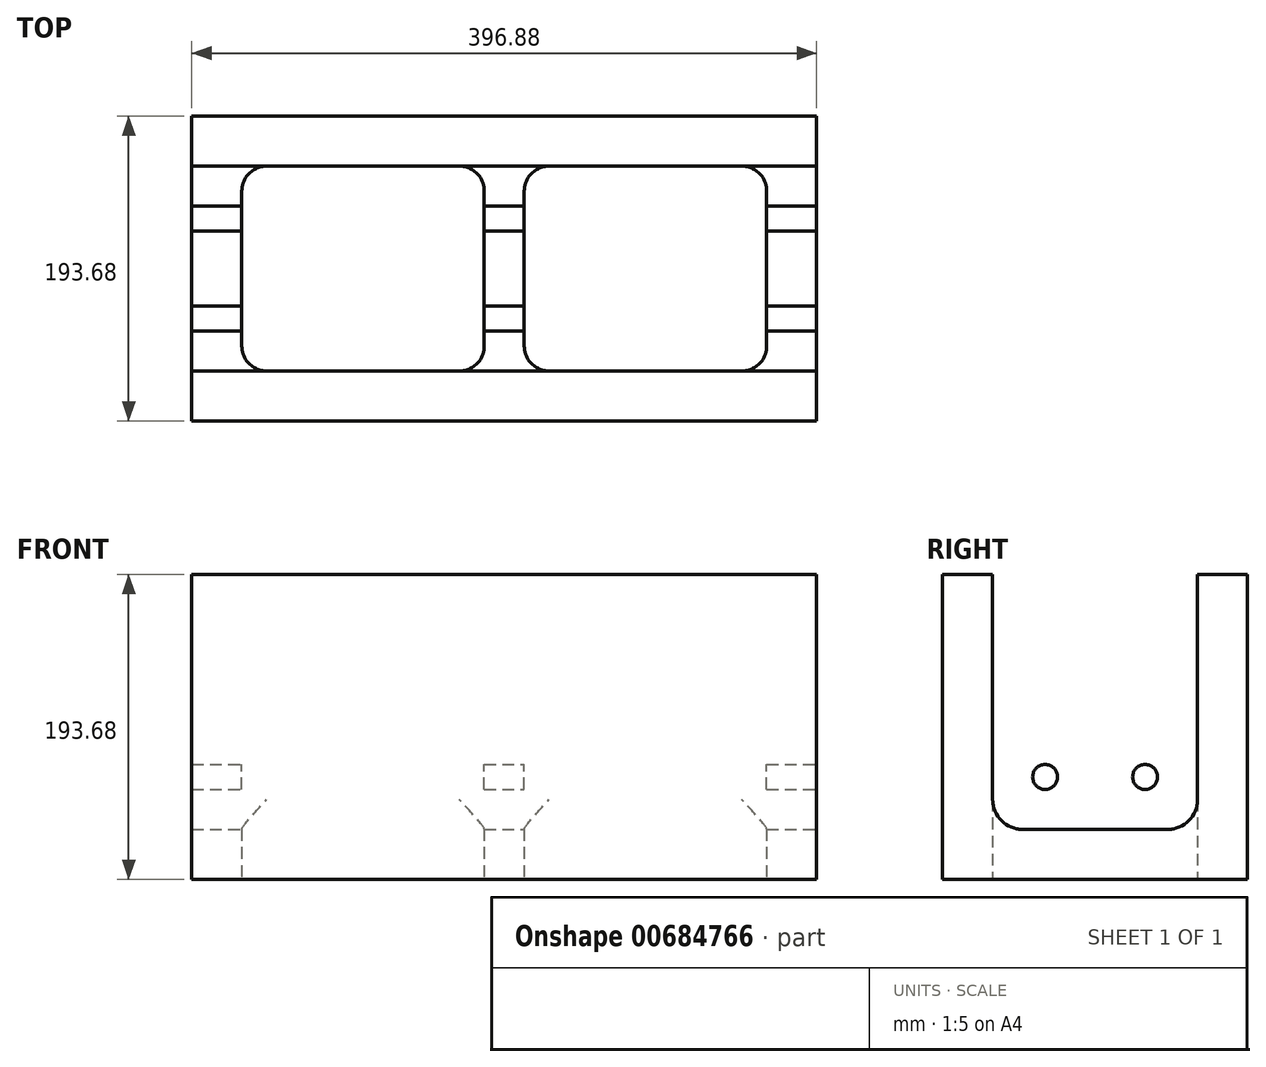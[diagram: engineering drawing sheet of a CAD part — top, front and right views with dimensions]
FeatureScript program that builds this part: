
annotation { "Feature Type Name" : "Feature", "Feature Type Description" : "" }
export const myFeature = defineFeature(function(context is Context, id is Id, definition is map)
    precondition{}
    {
        {
            var Q0;
            Q0=qCreatedBy(makeId("Top.planeOp"),FACE);
            var sketch = newSketch(context, id + "F0", { "sketchPlane" : qUnion([Q0])});
            skLineSegment(sketch, "E0.bottom", {"start": v(-198.44, 96.84) * mm, "end": v(198.44, 96.84) * mm});
            skLineSegment(sketch, "E0.top", {"start": v(-198.44, -96.84) * mm, "end": v(198.44, -96.84) * mm});
            skLineSegment(sketch, "E0.left", {"start": v(-198.44, 96.84) * mm, "end": v(-198.44, -96.84) * mm});
            skLineSegment(sketch, "E0.right", {"start": v(198.44, 96.84) * mm, "end": v(198.44, -96.84) * mm});
            skLineSegment(sketch, "E1.bottom", {"start": v(-150.81, 65.09) * mm, "end": v(-28.57, 65.09) * mm});
            skLineSegment(sketch, "E1.top", {"start": v(-150.81, -65.09) * mm, "end": v(-28.58, -65.09) * mm});
            skLineSegment(sketch, "E1.left", {"start": v(-166.69, 49.21) * mm, "end": v(-166.69, -49.21) * mm});
            skLineSegment(sketch, "E1.right", {"start": v(-12.7, 49.21) * mm, "end": v(-12.7, -49.21) * mm});
            skLineSegment(sketch, "E2", {"start": v(0, 96.84) * mm, "end": v(0, -96.84) * mm, "construction": true});
            skLineSegment(sketch, "E3.MirrorCS", {"start": v(166.69, 49.21) * mm, "end": v(166.69, -49.21) * mm});
            skLineSegment(sketch, "E4.MirrorCS", {"start": v(150.81, 65.09) * mm, "end": v(28.57, 65.09) * mm});
            skLineSegment(sketch, "E5.MirrorCS", {"start": v(150.81, -65.09) * mm, "end": v(28.57, -65.09) * mm});
            skLineSegment(sketch, "E6.MirrorCS", {"start": v(12.7, 49.21) * mm, "end": v(12.7, -49.21) * mm});
            skPoint(sketch, "E7.visualSharp", {"position": v(-166.69, 65.09) * mm});
            skArc(sketch, "E7.filletArc", {"start": v(-150.81, 65.09) * mm, "mid": v(-162.04, 60.44) * mm, "end": v(-166.69, 49.21) * mm});
            skPoint(sketch, "E8.visualSharp", {"position": v(-166.69, -65.09) * mm});
            skArc(sketch, "E8.filletArc", {"start": v(-166.69, -49.21) * mm, "mid": v(-162.04, -60.44) * mm, "end": v(-150.81, -65.09) * mm});
            skPoint(sketch, "E9.visualSharp", {"position": v(-12.7, -65.09) * mm});
            skArc(sketch, "E9.filletArc", {"start": v(-28.58, -65.09) * mm, "mid": v(-17.35, -60.44) * mm, "end": v(-12.7, -49.21) * mm});
            skPoint(sketch, "E10.visualSharp", {"position": v(-12.7, 65.09) * mm});
            skArc(sketch, "E10.filletArc", {"start": v(-12.7, 49.21) * mm, "mid": v(-17.35, 60.44) * mm, "end": v(-28.57, 65.09) * mm});
            skPoint(sketch, "E11.visualSharp", {"position": v(12.7, 65.09) * mm});
            skArc(sketch, "E11.filletArc", {"start": v(28.57, 65.09) * mm, "mid": v(17.35, 60.44) * mm, "end": v(12.7, 49.21) * mm});
            skPoint(sketch, "E12.visualSharp", {"position": v(12.7, -65.09) * mm});
            skArc(sketch, "E12.filletArc", {"start": v(12.7, -49.21) * mm, "mid": v(17.35, -60.44) * mm, "end": v(28.57, -65.09) * mm});
            skPoint(sketch, "E13.visualSharp", {"position": v(166.69, -65.09) * mm});
            skArc(sketch, "E13.filletArc", {"start": v(150.81, -65.09) * mm, "mid": v(162.04, -60.44) * mm, "end": v(166.69, -49.21) * mm});
            skPoint(sketch, "E14.visualSharp", {"position": v(166.69, 65.09) * mm});
            skArc(sketch, "E14.filletArc", {"start": v(166.69, 49.21) * mm, "mid": v(162.04, 60.44) * mm, "end": v(150.81, 65.09) * mm});
            skLineSegment(sketch, "E15", {"start": v(-12.7, 0) * mm, "end": v(12.7, 0) * mm});
            skSolve(sketch);
        }
        {
            var Q0;
            Q0=makeQuery(id+"F0.imprint","IMPRINT",FACE,{"disambiguationData":[TD([[makeQuery(id+"F0.imprint","IMPRINT",EDGE,{"derivedFrom":sQuery(id+"F0.wireOp",EDGE,"E0.bottom")}),-1.0]])]});
            extrude(context, id + "F1", {"entities" : qUnion([Q0]), "endBound" : BoundingType.SYMMETRIC, "depth" : 193.67 * mm, "offsetDistance" : 25.4 * mm});
        }
        {
            var Q0;
            Q0=makeQuery(id+"F1.opExtrude","SWEPT_FACE",FACE,{"disambiguationData":[OSD([sQuery(id+"F0.wireOp",EDGE,"E0.right")])]});
            var sketch = newSketch(context, id + "F2", { "sketchPlane" : qUnion([Q0])});
            skLineSegment(sketch, "E16", {"start": v(-65.09, 96.84) * mm, "end": v(-65.09, -46.04) * mm});
            skLineSegment(sketch, "E17", {"start": v(-46.04, -65.09) * mm, "end": v(46.04, -65.09) * mm});
            skLineSegment(sketch, "E18", {"start": v(65.09, -46.04) * mm, "end": v(65.09, 96.84) * mm});
            skLineSegment(sketch, "E19", {"start": v(65.09, 96.84) * mm, "end": v(-65.09, 96.84) * mm});
            skLineSegment(sketch, "E20", {"start": v(0, -65.09) * mm, "end": v(0, -96.84) * mm, "construction": true});
            skPoint(sketch, "E21.visualSharp", {"position": v(-65.09, -65.09) * mm});
            skArc(sketch, "E21.filletArc", {"start": v(-65.09, -46.04) * mm, "mid": v(-59.5, -59.5) * mm, "end": v(-46.04, -65.09) * mm});
            skPoint(sketch, "E22.visualSharp", {"position": v(65.09, -65.09) * mm});
            skArc(sketch, "E22.filletArc", {"start": v(46.04, -65.09) * mm, "mid": v(59.5, -59.5) * mm, "end": v(65.09, -46.04) * mm});
            skLineSegment(sketch, "E23", {"start": v(65.09, 25.4) * mm, "end": v(96.84, 25.4) * mm, "construction": true});
            skCircle(sketch, "E24", {"center": v(-31.75, -31.75) * mm, "radius": 7.94 * mm});
            skCircle(sketch, "E25", {"center": v(31.75, -31.75) * mm, "radius": 7.94 * mm});
            skSolve(sketch);
        }
        {
            var Q0;
            Q0=qSketchRegion(id+"F2",true);
            extrude(context, id + "F3", {"entities" : qUnion([Q0]), "operationType" : NewBodyOperationType.REMOVE, "endBound" : BoundingType.THROUGH_ALL, "oppositeDirection" : true, "depth" : 25.4 * mm, "offsetDistance" : 25.4 * mm});
        }
    });
